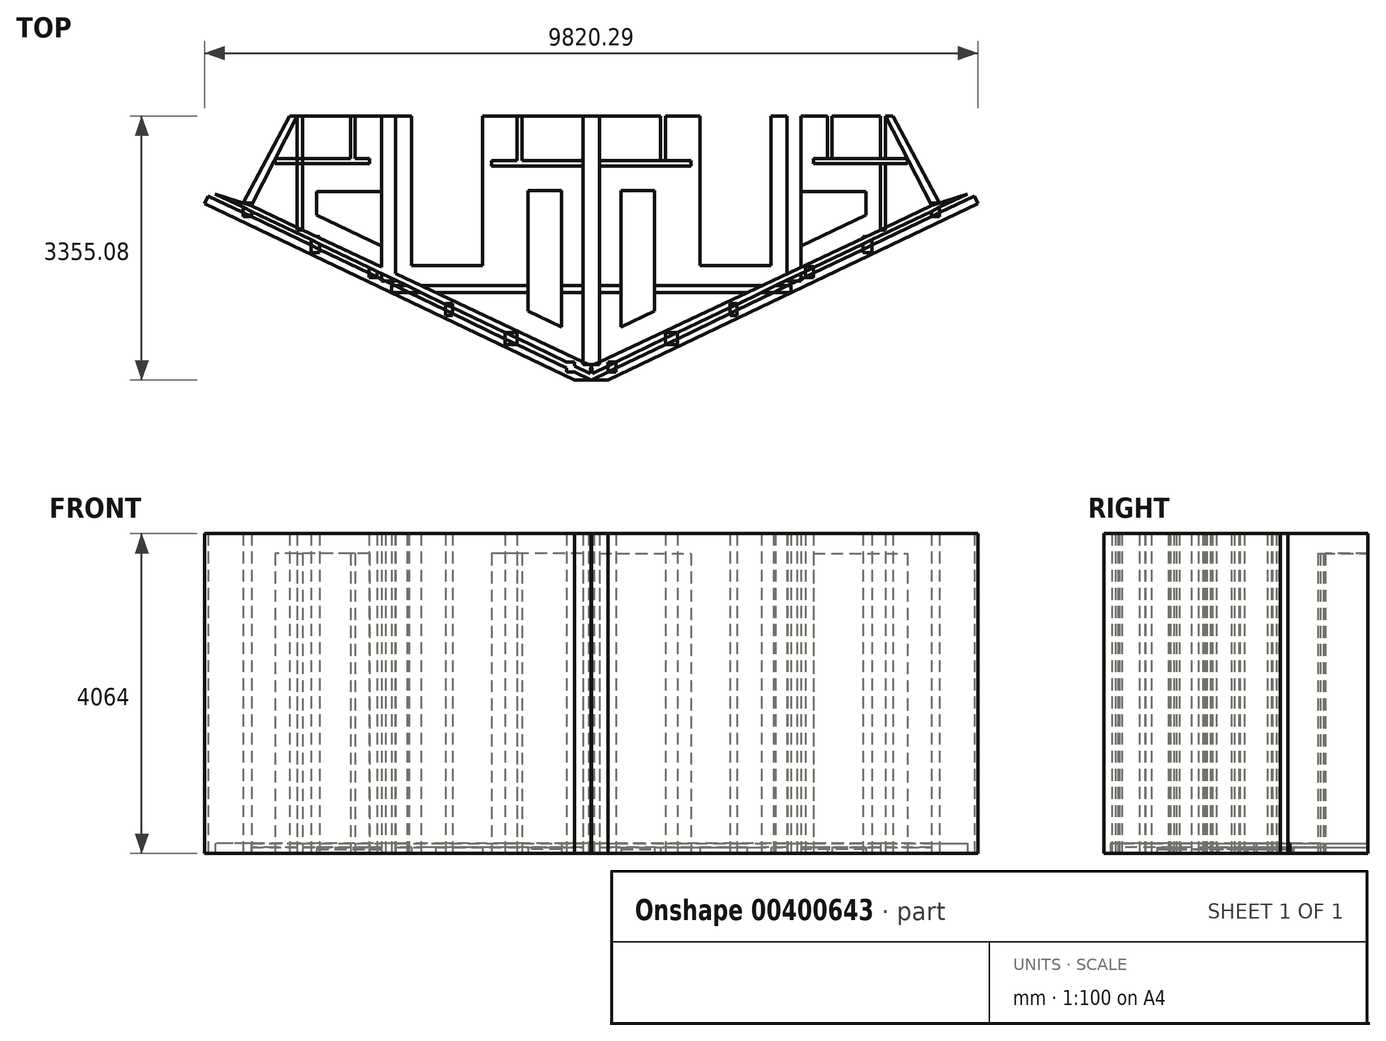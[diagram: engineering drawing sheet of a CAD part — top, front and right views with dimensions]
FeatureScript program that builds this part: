
annotation { "Feature Type Name" : "Feature", "Feature Type Description" : "" }
export const myFeature = defineFeature(function(context is Context, id is Id, definition is map)
    precondition{}
    {
        {
            var Q0;
            Q0=qCreatedBy(makeId("Top.planeOp"),FACE);
            var sketch = newSketch(context, id + "F0", { "sketchPlane" : qUnion([Q0])});
            skLineSegment(sketch, "E0", {"start": v(0, 0) * mm, "end": v(3734.31, 0) * mm});
            skLineSegment(sketch, "E1", {"start": v(3734.31, 0) * mm, "end": v(4319.25, -1139.54) * mm});
            skLineSegment(sketch, "E2", {"start": v(4319.25, -1139.54) * mm, "end": v(0, -3172.23) * mm});
            skLineSegment(sketch, "E3.bottom", {"start": v(1378.63, -1900) * mm, "end": v(2278.63, -1900) * mm});
            skLineSegment(sketch, "E3.top", {"start": v(1378.63, 0) * mm, "end": v(2278.63, 0) * mm});
            skLineSegment(sketch, "E3.left", {"start": v(1378.63, -1900) * mm, "end": v(1378.63, 0) * mm});
            skLineSegment(sketch, "E3.right", {"start": v(2278.63, -1900) * mm, "end": v(2278.63, 0) * mm});
            skLineSegment(sketch, "E4.bottom", {"start": v(3734.31, 0) * mm, "end": v(3668.02, 0) * mm});
            skLineSegment(sketch, "E4.top", {"start": v(3734.31, -1446.02) * mm, "end": v(3668.02, -1446.02) * mm});
            skLineSegment(sketch, "E4.left", {"start": v(3734.31, 0) * mm, "end": v(3734.31, -1446.02) * mm});
            skLineSegment(sketch, "E4.right", {"start": v(3668.02, 0) * mm, "end": v(3668.02, -1446.02) * mm});
            skLineSegment(sketch, "E5", {"start": v(12.4, -3268.41) * mm, "end": v(4773.75, -991.9) * mm});
            skLineSegment(sketch, "E6", {"start": v(4319.25, -1139.54) * mm, "end": v(4773.75, -991.9) * mm});
            skLineSegment(sketch, "E7", {"start": v(0, -3172.23) * mm, "end": v(12.4, -3268.41) * mm});
            skLineSegment(sketch, "E8.bottom", {"start": v(-2.48, -3156.82) * mm, "end": v(101.67, -3156.82) * mm});
            skLineSegment(sketch, "E8.top", {"start": v(-2.48, 0) * mm, "end": v(101.67, 0) * mm});
            skLineSegment(sketch, "E8.left", {"start": v(-2.48, -3156.82) * mm, "end": v(-2.48, 0) * mm});
            skLineSegment(sketch, "E8.right", {"start": v(101.67, -3156.82) * mm, "end": v(101.67, 0) * mm});
            skLineSegment(sketch, "E9.bottom", {"start": v(101.67, -567.84) * mm, "end": v(1262.25, -567.84) * mm});
            skLineSegment(sketch, "E9.top", {"start": v(101.67, -634.8) * mm, "end": v(1262.25, -634.8) * mm});
            skLineSegment(sketch, "E9.left", {"start": v(101.67, -567.84) * mm, "end": v(101.67, -634.8) * mm});
            skLineSegment(sketch, "E9.right", {"start": v(1262.25, -567.84) * mm, "end": v(1262.25, -634.8) * mm});
            skLineSegment(sketch, "E10.bottom", {"start": v(2817.13, -605.03) * mm, "end": v(4012.28, -605.03) * mm});
            skLineSegment(sketch, "E10.top", {"start": v(2817.13, -541.51) * mm, "end": v(4012.28, -541.51) * mm});
            skLineSegment(sketch, "E10.left", {"start": v(2817.13, -605.03) * mm, "end": v(2817.13, -541.51) * mm});
            skLineSegment(sketch, "E10.right", {"start": v(4012.28, -605.03) * mm, "end": v(4012.28, -541.51) * mm});
            skLineSegment(sketch, "E11.bottom", {"start": v(875.4, -567.84) * mm, "end": v(942.35, -567.84) * mm});
            skLineSegment(sketch, "E11.top", {"start": v(875.4, 0) * mm, "end": v(942.35, 0) * mm});
            skLineSegment(sketch, "E11.left", {"start": v(875.4, -567.84) * mm, "end": v(875.4, 0) * mm});
            skLineSegment(sketch, "E11.right", {"start": v(942.35, -567.84) * mm, "end": v(942.35, 0) * mm});
            skLineSegment(sketch, "E12.bottom", {"start": v(2995.68, -541.51) * mm, "end": v(3055.2, -541.51) * mm});
            skLineSegment(sketch, "E12.top", {"start": v(2995.68, 0) * mm, "end": v(3055.2, 0) * mm});
            skLineSegment(sketch, "E12.left", {"start": v(2995.68, -541.51) * mm, "end": v(2995.68, 0) * mm});
            skLineSegment(sketch, "E12.right", {"start": v(3055.2, -541.51) * mm, "end": v(3055.2, 0) * mm});
            skPoint(sketch, "E13.oppositeSnap0", {"position": v(2159.62, -2155.89) * mm});
            skLineSegment(sketch, "E13.bottom", {"start": v(101.67, -2241.75) * mm, "end": v(2534.42, -2241.75) * mm});
            skLineSegment(sketch, "E13.top", {"start": v(101.67, -2155.89) * mm, "end": v(2534.42, -2155.89) * mm});
            skLineSegment(sketch, "E13.left", {"start": v(101.67, -2241.75) * mm, "end": v(101.67, -2155.89) * mm});
            skLineSegment(sketch, "E13.right", {"start": v(2534.42, -2241.75) * mm, "end": v(2534.42, -2155.89) * mm});
            skLineSegment(sketch, "E14", {"start": v(4907.66, -1110.93) * mm, "end": v(4863.02, -1014.21) * mm});
            skLineSegment(sketch, "E15", {"start": v(4863.02, -1014.21) * mm, "end": v(0, -3355.08) * mm});
            skLineSegment(sketch, "E16", {"start": v(0, -3355.08) * mm, "end": v(210.83, -3355.08) * mm});
            skLineSegment(sketch, "E17", {"start": v(210.83, -3355.08) * mm, "end": v(4907.66, -1110.93) * mm});
            skLineSegment(sketch, "E18.bottom", {"start": v(210.83, -3253.6) * mm, "end": v(312.92, -3253.6) * mm});
            skLineSegment(sketch, "E18.top", {"start": v(210.83, -3124.73) * mm, "end": v(312.92, -3124.73) * mm});
            skLineSegment(sketch, "E18.left", {"start": v(210.83, -3253.6) * mm, "end": v(210.83, -3124.73) * mm});
            skLineSegment(sketch, "E18.right", {"start": v(312.92, -3253.6) * mm, "end": v(312.92, -3124.73) * mm});
            skLineSegment(sketch, "E19.bottom", {"start": v(942.92, -2901.2) * mm, "end": v(1090.07, -2901.2) * mm});
            skLineSegment(sketch, "E19.top", {"start": v(942.92, -2753.15) * mm, "end": v(1090.07, -2753.15) * mm});
            skLineSegment(sketch, "E19.left", {"start": v(942.92, -2901.2) * mm, "end": v(942.92, -2753.15) * mm});
            skLineSegment(sketch, "E19.right", {"start": v(1090.07, -2901.2) * mm, "end": v(1090.07, -2753.15) * mm});
            skLineSegment(sketch, "E20.bottom", {"start": v(1758.25, -2534.14) * mm, "end": v(1845.43, -2534.14) * mm});
            skLineSegment(sketch, "E20.top", {"start": v(1758.25, -2381.58) * mm, "end": v(1845.43, -2381.58) * mm});
            skLineSegment(sketch, "E20.left", {"start": v(1758.25, -2534.14) * mm, "end": v(1758.25, -2381.58) * mm});
            skLineSegment(sketch, "E20.right", {"start": v(1845.43, -2534.14) * mm, "end": v(1845.43, -2381.58) * mm});
            skLineSegment(sketch, "E21.bottom", {"start": v(2717.22, -2054.65) * mm, "end": v(2818.93, -2054.65) * mm});
            skLineSegment(sketch, "E21.top", {"start": v(2717.22, -1909.36) * mm, "end": v(2818.93, -1909.36) * mm});
            skLineSegment(sketch, "E21.left", {"start": v(2717.22, -2054.65) * mm, "end": v(2717.22, -1909.36) * mm});
            skLineSegment(sketch, "E21.right", {"start": v(2818.93, -2054.65) * mm, "end": v(2818.93, -1909.36) * mm});
            skLineSegment(sketch, "E22.bottom", {"start": v(3450.98, -1735) * mm, "end": v(3559.95, -1735) * mm});
            skLineSegment(sketch, "E22.top", {"start": v(3450.98, -1531.58) * mm, "end": v(3559.95, -1531.58) * mm});
            skLineSegment(sketch, "E22.left", {"start": v(3450.98, -1735) * mm, "end": v(3450.98, -1531.58) * mm});
            skLineSegment(sketch, "E22.right", {"start": v(3559.95, -1735) * mm, "end": v(3559.95, -1531.58) * mm});
            skLineSegment(sketch, "E23.bottom", {"start": v(2484.75, -2098.24) * mm, "end": v(2659.1, -2098.24) * mm});
            skLineSegment(sketch, "E23.top", {"start": v(2484.75, 0) * mm, "end": v(2659.1, 0) * mm});
            skLineSegment(sketch, "E23.left", {"start": v(2484.75, -2098.24) * mm, "end": v(2484.75, 0) * mm});
            skLineSegment(sketch, "E23.right", {"start": v(2659.1, -2098.24) * mm, "end": v(2659.1, 0) * mm});
            skLineSegment(sketch, "E24", {"start": v(4422.89, -1105.87) * mm, "end": v(3828.76, 0) * mm});
            skLineSegment(sketch, "E25", {"start": v(3734.31, 0) * mm, "end": v(3828.76, 0) * mm});
            skLineSegment(sketch, "E26.bottom", {"start": v(4315.69, -1277.68) * mm, "end": v(4422.89, -1277.68) * mm});
            skLineSegment(sketch, "E26.top", {"start": v(4315.69, -1105.87) * mm, "end": v(4422.89, -1105.87) * mm});
            skLineSegment(sketch, "E26.left", {"start": v(4315.69, -1277.68) * mm, "end": v(4315.69, -1105.87) * mm});
            skLineSegment(sketch, "E26.right", {"start": v(4422.89, -1277.68) * mm, "end": v(4422.89, -1105.87) * mm});
            skLineSegment(sketch, "E27.MirrorCS", {"start": v(-3739.28, 0) * mm, "end": v(-3672.98, 0) * mm});
            skLineSegment(sketch, "E28.MirrorCS", {"start": v(-4320.65, -1105.87) * mm, "end": v(-4427.85, -1105.87) * mm});
            skLineSegment(sketch, "E29.MirrorCS", {"start": v(-1763.22, -2534.14) * mm, "end": v(-1850.4, -2534.14) * mm});
            skLineSegment(sketch, "E30.MirrorCS", {"start": v(-4017.24, -605.03) * mm, "end": v(-4017.24, -541.51) * mm});
            skLineSegment(sketch, "E31.MirrorCS", {"start": v(-1095.04, -2901.2) * mm, "end": v(-1095.04, -2753.15) * mm});
            skLineSegment(sketch, "E32.MirrorCS", {"start": v(-2823.9, -2054.65) * mm, "end": v(-2823.9, -1909.36) * mm});
            skLineSegment(sketch, "E33.MirrorCS", {"start": v(-3455.95, -1735) * mm, "end": v(-3564.92, -1735) * mm});
            skLineSegment(sketch, "E34.MirrorCS", {"start": v(-215.8, -3253.6) * mm, "end": v(-317.88, -3253.6) * mm});
            skLineSegment(sketch, "E35.MirrorCS", {"start": v(-880.36, -567.84) * mm, "end": v(-947.31, -567.84) * mm});
            skLineSegment(sketch, "E36.MirrorCS", {"start": v(-3739.28, 0) * mm, "end": v(-3833.72, 0) * mm});
            skLineSegment(sketch, "E37.MirrorCS", {"start": v(-1763.22, -2381.58) * mm, "end": v(-1850.4, -2381.58) * mm});
            skLineSegment(sketch, "E38.MirrorCS", {"start": v(-2822.1, -605.03) * mm, "end": v(-2822.1, -541.51) * mm});
            skLineSegment(sketch, "E39.MirrorCS", {"start": v(-2722.2, -2054.65) * mm, "end": v(-2722.2, -1909.36) * mm});
            skLineSegment(sketch, "E40.MirrorCS", {"start": v(-947.89, -2901.2) * mm, "end": v(-947.89, -2753.15) * mm});
            skLineSegment(sketch, "E41.MirrorCS", {"start": v(-2489.71, 0) * mm, "end": v(-2664.07, 0) * mm});
            skLineSegment(sketch, "E42.MirrorCS", {"start": v(-947.89, -2753.15) * mm, "end": v(-1095.04, -2753.15) * mm});
            skLineSegment(sketch, "E43.MirrorCS", {"start": v(-4320.65, -1277.68) * mm, "end": v(-4320.65, -1105.87) * mm});
            skLineSegment(sketch, "E44.MirrorCS", {"start": v(-3000.65, 0) * mm, "end": v(-3060.16, 0) * mm});
            skLineSegment(sketch, "E45.MirrorCS", {"start": v(-4912.63, -1110.93) * mm, "end": v(-4867.99, -1014.21) * mm});
            skLineSegment(sketch, "E46.MirrorCS", {"start": v(-215.8, -3124.73) * mm, "end": v(-317.88, -3124.73) * mm});
            skLineSegment(sketch, "E47.MirrorCS", {"start": v(-4.97, -3172.23) * mm, "end": v(-17.36, -3268.41) * mm});
            skLineSegment(sketch, "E48.MirrorCS", {"start": v(-2722.2, -2054.65) * mm, "end": v(-2823.9, -2054.65) * mm});
            skLineSegment(sketch, "E49.MirrorCS", {"start": v(-106.64, -567.84) * mm, "end": v(-106.64, -634.8) * mm});
            skLineSegment(sketch, "E50.MirrorCS", {"start": v(-2.48, 0) * mm, "end": v(-106.64, 0) * mm});
            skLineSegment(sketch, "E51.MirrorCS", {"start": v(-2.48, -3156.82) * mm, "end": v(-106.64, -3156.82) * mm});
            skLineSegment(sketch, "E52.MirrorCS", {"start": v(-317.88, -3253.6) * mm, "end": v(-317.88, -3124.73) * mm});
            skLineSegment(sketch, "E53.MirrorCS", {"start": v(-880.36, 0) * mm, "end": v(-947.31, 0) * mm});
            skLineSegment(sketch, "E54.MirrorCS", {"start": v(-4427.85, -1277.68) * mm, "end": v(-4427.85, -1105.87) * mm});
            skLineSegment(sketch, "E55.MirrorCS", {"start": v(-2722.2, -1909.36) * mm, "end": v(-2823.9, -1909.36) * mm});
            skLineSegment(sketch, "E56.MirrorCS", {"start": v(-4320.65, -1277.68) * mm, "end": v(-4427.85, -1277.68) * mm});
            skLineSegment(sketch, "E57.MirrorCS", {"start": v(-1763.22, -2534.14) * mm, "end": v(-1763.22, -2381.58) * mm});
            skLineSegment(sketch, "E58.MirrorCS", {"start": v(-106.64, -2241.75) * mm, "end": v(-106.64, -2155.89) * mm});
            skLineSegment(sketch, "E59.MirrorCS", {"start": v(-3739.28, -1446.02) * mm, "end": v(-3672.98, -1446.02) * mm});
            skLineSegment(sketch, "E60.MirrorCS", {"start": v(-3455.95, -1531.58) * mm, "end": v(-3564.92, -1531.58) * mm});
            skLineSegment(sketch, "E61.MirrorCS", {"start": v(-3000.65, -541.51) * mm, "end": v(-3060.16, -541.51) * mm});
            skLineSegment(sketch, "E62.MirrorCS", {"start": v(-215.8, -3253.6) * mm, "end": v(-215.8, -3124.73) * mm});
            skLineSegment(sketch, "E63.MirrorCS", {"start": v(-1267.22, -567.84) * mm, "end": v(-1267.22, -634.8) * mm});
            skLineSegment(sketch, "E64.MirrorCS", {"start": v(-1850.4, -2534.14) * mm, "end": v(-1850.4, -2381.58) * mm});
            skLineSegment(sketch, "E65.MirrorCS", {"start": v(-2489.71, -2098.24) * mm, "end": v(-2664.07, -2098.24) * mm});
            skLineSegment(sketch, "E66.MirrorCS", {"start": v(-947.89, -2901.2) * mm, "end": v(-1095.04, -2901.2) * mm});
            skLineSegment(sketch, "E67.MirrorCS", {"start": v(-2539.4, -2241.75) * mm, "end": v(-2539.4, -2155.89) * mm});
            skLineSegment(sketch, "E68.MirrorCS", {"start": v(-3564.92, -1735) * mm, "end": v(-3564.92, -1531.58) * mm});
            skLineSegment(sketch, "E69.MirrorCS", {"start": v(-3455.95, -1735) * mm, "end": v(-3455.95, -1531.58) * mm});
            skLineSegment(sketch, "E70.MirrorCS", {"start": v(-106.64, -2241.75) * mm, "end": v(-2539.4, -2241.75) * mm});
            skLineSegment(sketch, "E71.MirrorCS", {"start": v(-4427.85, -1105.87) * mm, "end": v(-3833.72, 0) * mm});
            skLineSegment(sketch, "E72.MirrorCS", {"start": v(-106.64, -567.84) * mm, "end": v(-1267.22, -567.84) * mm});
            skLineSegment(sketch, "E73.MirrorCS", {"start": v(-3060.16, -541.51) * mm, "end": v(-3060.16, 0) * mm});
            skLineSegment(sketch, "E74.MirrorCS", {"start": v(-2664.07, -2098.24) * mm, "end": v(-2664.07, 0) * mm});
            skLineSegment(sketch, "E75.MirrorCS", {"start": v(-106.64, -634.8) * mm, "end": v(-1267.22, -634.8) * mm});
            skLineSegment(sketch, "E76.MirrorCS", {"start": v(-106.64, -3156.82) * mm, "end": v(-106.64, 0) * mm});
            skLineSegment(sketch, "E77.MirrorCS", {"start": v(-4.97, -3355.08) * mm, "end": v(-215.8, -3355.08) * mm});
            skLineSegment(sketch, "E78.MirrorCS", {"start": v(-106.64, -2155.89) * mm, "end": v(-2539.4, -2155.89) * mm});
            skLineSegment(sketch, "E79.MirrorCS", {"start": v(-215.8, -3355.08) * mm, "end": v(-4912.63, -1110.93) * mm});
            skLineSegment(sketch, "E80.MirrorCS", {"start": v(-3000.65, -541.51) * mm, "end": v(-3000.65, 0) * mm});
            skLineSegment(sketch, "E81.MirrorCS", {"start": v(-2489.71, -2098.24) * mm, "end": v(-2489.71, 0) * mm});
            skPoint(sketch, "E82.MirrorP", {"position": v(-2164.6, -2155.89) * mm});
            skLineSegment(sketch, "E83.MirrorCS", {"start": v(-2822.1, -605.03) * mm, "end": v(-4017.24, -605.03) * mm});
            skLineSegment(sketch, "E84.MirrorCS", {"start": v(-4.97, 0) * mm, "end": v(-3739.28, 0) * mm});
            skLineSegment(sketch, "E85.MirrorCS", {"start": v(-3739.28, 0) * mm, "end": v(-4324.22, -1139.54) * mm});
            skLineSegment(sketch, "E86.MirrorCS", {"start": v(-4324.22, -1139.54) * mm, "end": v(-4.97, -3172.23) * mm});
            skLineSegment(sketch, "E87.MirrorCS", {"start": v(-4867.99, -1014.21) * mm, "end": v(-4.97, -3355.08) * mm});
            skLineSegment(sketch, "E88.MirrorCS", {"start": v(-2822.1, -541.51) * mm, "end": v(-4017.24, -541.51) * mm});
            skLineSegment(sketch, "E89.MirrorCS", {"start": v(-1383.6, -1900) * mm, "end": v(-2283.6, -1900) * mm});
            skLineSegment(sketch, "E90.MirrorCS", {"start": v(-947.31, -567.84) * mm, "end": v(-947.31, 0) * mm});
            skLineSegment(sketch, "E91.MirrorCS", {"start": v(-1383.6, 0) * mm, "end": v(-2283.6, 0) * mm});
            skLineSegment(sketch, "E92.MirrorCS", {"start": v(-4324.22, -1139.54) * mm, "end": v(-4778.71, -991.9) * mm});
            skLineSegment(sketch, "E93.MirrorCS", {"start": v(-17.36, -3268.41) * mm, "end": v(-4778.71, -991.9) * mm});
            skLineSegment(sketch, "E94.MirrorCS", {"start": v(-3739.28, 0) * mm, "end": v(-3739.28, -1446.02) * mm});
            skLineSegment(sketch, "E95.MirrorCS", {"start": v(-2283.6, -1900) * mm, "end": v(-2283.6, 0) * mm});
            skLineSegment(sketch, "E96.MirrorCS", {"start": v(-1383.6, -1900) * mm, "end": v(-1383.6, 0) * mm});
            skLineSegment(sketch, "E97.MirrorCS", {"start": v(-3672.98, 0) * mm, "end": v(-3672.98, -1446.02) * mm});
            skLineSegment(sketch, "E98.MirrorCS", {"start": v(-880.36, -567.84) * mm, "end": v(-880.36, 0) * mm});
            skLineSegment(sketch, "E99", {"start": v(-383, -2677.78) * mm, "end": v(-383, -949.63) * mm});
            skLineSegment(sketch, "E100", {"start": v(-383, -949.63) * mm, "end": v(-804.7, -949.63) * mm});
            skLineSegment(sketch, "E101", {"start": v(-804.7, -949.63) * mm, "end": v(-804.7, -2476.29) * mm});
            skLineSegment(sketch, "E102", {"start": v(-804.7, -2476.29) * mm, "end": v(-383, -2677.78) * mm});
            skPoint(sketch, "E103.endSnap0", {"position": v(-3419.67, -605.03) * mm});
            skLineSegment(sketch, "E104", {"start": v(-3492.38, -1256.21) * mm, "end": v(-2664.07, -1654.93) * mm});
            skLineSegment(sketch, "E105", {"start": v(-3492.38, -1256.21) * mm, "end": v(-3492.38, -959.85) * mm});
            skLineSegment(sketch, "E106", {"start": v(-3492.38, -959.85) * mm, "end": v(-2664.07, -959.85) * mm});
            skLineSegment(sketch, "E107.MirrorCS", {"start": v(799.73, -949.63) * mm, "end": v(799.73, -2476.29) * mm});
            skLineSegment(sketch, "E108.MirrorCS", {"start": v(378.03, -2677.78) * mm, "end": v(378.03, -949.63) * mm});
            skLineSegment(sketch, "E109.MirrorCS", {"start": v(378.03, -949.63) * mm, "end": v(799.73, -949.63) * mm});
            skLineSegment(sketch, "E110.MirrorCS", {"start": v(799.73, -2476.29) * mm, "end": v(378.03, -2677.78) * mm});
            skLineSegment(sketch, "E111.MirrorCS", {"start": v(3487.42, -1256.21) * mm, "end": v(2659.1, -1654.93) * mm});
            skLineSegment(sketch, "E112.MirrorCS", {"start": v(3487.42, -1256.21) * mm, "end": v(3487.42, -959.85) * mm});
            skLineSegment(sketch, "E113.MirrorCS", {"start": v(3487.42, -959.85) * mm, "end": v(2659.1, -959.85) * mm});
            skSolve(sketch);
        }
        {
            var Q0;
            {var subQ1=sQuery(id+"F0.wireOp",EDGE,"E28.MirrorCS");Q0=makeQuery(id+"F0.imprint","IMPRINT",FACE,{"disambiguationData":[TD([[makeQuery(id+"F0.imprint","IMPRINT",EDGE,{"derivedFrom":subQ1}),-1.0]])]});}
            var Q1;
            {var subQ5=sQuery(id+"F0.wireOp",EDGE,"E29.MirrorCS");Q1=makeQuery(id+"F0.imprint","IMPRINT",FACE,{"disambiguationData":[TD([[makeQuery(id+"F0.imprint","IMPRINT",EDGE,{"derivedFrom":subQ5}),1.0]])]});}
            var Q2;
            {var subQ20=sQuery(id+"F0.wireOp",EDGE,"E13.right");Q2=makeQuery(id+"F0.imprint","IMPRINT",FACE,{"disambiguationData":[TD([[makeQuery(id+"F0.imprint","IMPRINT",EDGE,{"derivedFrom":subQ20}),-1.0]])]});}
            var Q3;
            Q3=makeQuery(id+"F0.imprint","IMPRINT",FACE,{"disambiguationData":[TD([[makeQuery(id+"F0.imprint","IMPRINT",EDGE,{"derivedFrom":sQuery(id+"F0.wireOp",EDGE,"E24")}),1.0]])]});
            var Q4;
            {var subQ5=sQuery(id+"F0.wireOp",EDGE,"E8.left");Q4=makeQuery(id+"F0.imprint","IMPRINT",FACE,{"disambiguationData":[TD([[makeQuery(id+"F0.imprint","IMPRINT",EDGE,{"derivedFrom":subQ5}),1.0]])]});}
            var Q5;
            {var subQ3=sQuery(id+"F0.wireOp",EDGE,"E8.left");Q5=makeQuery(id+"F0.imprint","IMPRINT",FACE,{"disambiguationData":[TD([[makeQuery(id+"F0.imprint","IMPRINT",EDGE,{"derivedFrom":subQ3}),-1.0]])]});}
            extrude(context, id + "F1", {"entities" : qUnion([Q0, Q1, Q2, Q3, Q4, Q5]), "depth" : 4064 * mm, "offsetDistance" : 25.4 * mm});
        }
        {
            var Q0;
            {var subQ1=sQuery(id+"F0.wireOp",EDGE,"E5");var subQ3=sQuery(id+"F0.wireOp",EDGE,"E18.left");var subQ4=makeQuery(id+"F0.imprint","INTERSECT",VERTEX,{"derivedFrom":[subQ1,subQ3]});Q0=makeQuery(id+"F0.imprint","IMPRINT",FACE,{"disambiguationData":[TD([[makeQuery(id+"F0.imprint","IMPRINT",EDGE,{"disambiguationData":[TD([[subQ4,-1.0]])],"derivedFrom":subQ1}),-1.0]])]});}
            var Q1;
            {var subQ1=sQuery(id+"F0.wireOp",EDGE,"E5");var subQ3=sQuery(id+"F0.wireOp",EDGE,"E19.left");var subQ4=makeQuery(id+"F0.imprint","INTERSECT",VERTEX,{"derivedFrom":[subQ1,subQ3]});Q1=makeQuery(id+"F0.imprint","IMPRINT",FACE,{"disambiguationData":[TD([[makeQuery(id+"F0.imprint","IMPRINT",EDGE,{"disambiguationData":[TD([[subQ4,-1.0]])],"derivedFrom":subQ1}),-1.0]])]});}
            var Q2;
            {var subQ0=sQuery(id+"F0.wireOp",EDGE,"E20.left");var subQ1=sQuery(id+"F0.wireOp",EDGE,"E5");var subQ2=makeQuery(id+"F0.imprint","INTERSECT",VERTEX,{"derivedFrom":[subQ1,subQ0]});Q2=makeQuery(id+"F0.imprint","IMPRINT",FACE,{"disambiguationData":[TD([[makeQuery(id+"F0.imprint","IMPRINT",EDGE,{"disambiguationData":[TD([[subQ2,-1.0]])],"derivedFrom":subQ1}),-1.0]])]});}
            var Q3;
            {var subQ0=sQuery(id+"F0.wireOp",EDGE,"E13.bottom");var subQ1=sQuery(id+"F0.wireOp",EDGE,"E5");var subQ2=makeQuery(id+"F0.imprint","INTERSECT",VERTEX,{"derivedFrom":[subQ1,subQ0]});Q3=makeQuery(id+"F0.imprint","IMPRINT",FACE,{"disambiguationData":[TD([[makeQuery(id+"F0.imprint","IMPRINT",EDGE,{"disambiguationData":[TD([[subQ2,-1.0]])],"derivedFrom":subQ1}),-1.0]])]});}
            var Q4;
            {var subQ0=sQuery(id+"F0.wireOp",EDGE,"E21.left");var subQ1=sQuery(id+"F0.wireOp",EDGE,"E5");var subQ2=makeQuery(id+"F0.imprint","INTERSECT",VERTEX,{"derivedFrom":[subQ1,subQ0]});Q4=makeQuery(id+"F0.imprint","IMPRINT",FACE,{"disambiguationData":[TD([[makeQuery(id+"F0.imprint","IMPRINT",EDGE,{"disambiguationData":[TD([[subQ2,-1.0]])],"derivedFrom":subQ1}),-1.0]])]});}
            var Q5;
            {var subQ0=sQuery(id+"F0.wireOp",EDGE,"E22.left");var subQ1=sQuery(id+"F0.wireOp",EDGE,"E5");var subQ2=makeQuery(id+"F0.imprint","INTERSECT",VERTEX,{"derivedFrom":[subQ1,subQ0]});Q5=makeQuery(id+"F0.imprint","IMPRINT",FACE,{"disambiguationData":[TD([[makeQuery(id+"F0.imprint","IMPRINT",EDGE,{"disambiguationData":[TD([[subQ2,-1.0]])],"derivedFrom":subQ1}),-1.0]])]});}
            var Q6;
            {var subQ0=sQuery(id+"F0.wireOp",EDGE,"E26.right");var subQ1=sQuery(id+"F0.wireOp",EDGE,"E5");var subQ2=makeQuery(id+"F0.imprint","INTERSECT",VERTEX,{"derivedFrom":[subQ1,subQ0]});Q6=makeQuery(id+"F0.imprint","IMPRINT",FACE,{"disambiguationData":[TD([[makeQuery(id+"F0.imprint","IMPRINT",EDGE,{"disambiguationData":[TD([[subQ2,1.0]])],"derivedFrom":subQ1}),-1.0]])]});}
            var Q7;
            {var subQ1=sQuery(id+"F0.wireOp",EDGE,"E31.MirrorCS");var subQ3=sQuery(id+"F0.wireOp",EDGE,"E87.MirrorCS");var subQ4=makeQuery(id+"F0.imprint","INTERSECT",VERTEX,{"derivedFrom":[subQ1,subQ3]});Q7=makeQuery(id+"F0.imprint","IMPRINT",FACE,{"disambiguationData":[TD([[makeQuery(id+"F0.imprint","IMPRINT",EDGE,{"disambiguationData":[TD([[subQ4,-1.0]])],"derivedFrom":subQ1}),-1.0]])]});}
            var Q8;
            {var subQ0=sQuery(id+"F0.wireOp",EDGE,"E87.MirrorCS");var subQ1=sQuery(id+"F0.wireOp",EDGE,"E57.MirrorCS");var subQ2=makeQuery(id+"F0.imprint","INTERSECT",VERTEX,{"derivedFrom":[subQ1,subQ0]});Q8=makeQuery(id+"F0.imprint","IMPRINT",FACE,{"disambiguationData":[TD([[makeQuery(id+"F0.imprint","IMPRINT",EDGE,{"disambiguationData":[TD([[subQ2,-1.0]])],"derivedFrom":subQ1}),1.0]])]});}
            var Q9;
            {var subQ0=sQuery(id+"F0.wireOp",EDGE,"E93.MirrorCS");var subQ1=sQuery(id+"F0.wireOp",EDGE,"E70.MirrorCS");var subQ2=makeQuery(id+"F0.imprint","INTERSECT",VERTEX,{"derivedFrom":[subQ1,subQ0]});Q9=makeQuery(id+"F0.imprint","IMPRINT",FACE,{"disambiguationData":[TD([[makeQuery(id+"F0.imprint","IMPRINT",EDGE,{"disambiguationData":[TD([[subQ2,-1.0]])],"derivedFrom":subQ1}),-1.0]])]});}
            var Q10;
            {var subQ0=sQuery(id+"F0.wireOp",EDGE,"E87.MirrorCS");var subQ1=sQuery(id+"F0.wireOp",EDGE,"E32.MirrorCS");var subQ2=makeQuery(id+"F0.imprint","INTERSECT",VERTEX,{"derivedFrom":[subQ1,subQ0]});Q10=makeQuery(id+"F0.imprint","IMPRINT",FACE,{"disambiguationData":[TD([[makeQuery(id+"F0.imprint","IMPRINT",EDGE,{"disambiguationData":[TD([[subQ2,-1.0]])],"derivedFrom":subQ1}),-1.0]])]});}
            var Q11;
            {var subQ1=sQuery(id+"F0.wireOp",EDGE,"E65.MirrorCS");var subQ5=sQuery(id+"F0.wireOp",EDGE,"E81.MirrorCS");var subQ6=makeQuery(id+"F0.imprint","INTERSECT",VERTEX,{"derivedFrom":[subQ1,subQ5]});Q11=makeQuery(id+"F0.imprint","IMPRINT",FACE,{"disambiguationData":[TD([[makeQuery(id+"F0.imprint","IMPRINT",EDGE,{"disambiguationData":[TD([[subQ6,-1.0]])],"derivedFrom":subQ1}),-1.0]])]});}
            var Q12;
            {var subQ0=sQuery(id+"F0.wireOp",EDGE,"E23.left");var subQ3=sQuery(id+"F0.wireOp",EDGE,"E5");var subQ4=makeQuery(id+"F0.imprint","INTERSECT",VERTEX,{"derivedFrom":[subQ3,subQ0]});Q12=makeQuery(id+"F0.imprint","IMPRINT",FACE,{"disambiguationData":[TD([[makeQuery(id+"F0.imprint","IMPRINT",EDGE,{"disambiguationData":[TD([[subQ4,-1.0]])],"derivedFrom":subQ3}),-1.0]])]});}
            var Q13;
            {var subQ0=sQuery(id+"F0.wireOp",EDGE,"E87.MirrorCS");var subQ1=sQuery(id+"F0.wireOp",EDGE,"E68.MirrorCS");var subQ2=makeQuery(id+"F0.imprint","INTERSECT",VERTEX,{"derivedFrom":[subQ1,subQ0]});Q13=makeQuery(id+"F0.imprint","IMPRINT",FACE,{"disambiguationData":[TD([[makeQuery(id+"F0.imprint","IMPRINT",EDGE,{"disambiguationData":[TD([[subQ2,-1.0]])],"derivedFrom":subQ1}),-1.0]])]});}
            var Q14;
            {var subQ0=sQuery(id+"F0.wireOp",EDGE,"E87.MirrorCS");var subQ5=sQuery(id+"F0.wireOp",EDGE,"E54.MirrorCS");var subQ6=makeQuery(id+"F0.imprint","INTERSECT",VERTEX,{"derivedFrom":[subQ5,subQ0]});Q14=makeQuery(id+"F0.imprint","IMPRINT",FACE,{"disambiguationData":[TD([[makeQuery(id+"F0.imprint","IMPRINT",EDGE,{"disambiguationData":[TD([[subQ6,-1.0]])],"derivedFrom":subQ5}),-1.0]])]});}
            extrude(context, id + "F2", {"entities" : qUnion([Q0, Q1, Q2, Q3, Q4, Q5, Q6, Q7, Q8, Q9, Q10, Q11, Q12, Q13, Q14]), "depth" : 4064 * mm, "offsetDistance" : 25.4 * mm});
        }
        {
            var Q0;
            {var subQ4=sQuery(id+"F0.wireOp",EDGE,"E38.MirrorCS");Q0=makeQuery(id+"F0.imprint","IMPRINT",FACE,{"disambiguationData":[TD([[makeQuery(id+"F0.imprint","IMPRINT",EDGE,{"derivedFrom":subQ4}),1.0]])]});}
            var Q1;
            {var subQ0=sQuery(id+"F0.wireOp",EDGE,"E30.MirrorCS");Q1=makeQuery(id+"F0.imprint","IMPRINT",FACE,{"disambiguationData":[TD([[makeQuery(id+"F0.imprint","IMPRINT",EDGE,{"derivedFrom":subQ0}),-1.0]])]});}
            var Q2;
            {var subQ0=sQuery(id+"F0.wireOp",EDGE,"E73.MirrorCS");Q2=makeQuery(id+"F0.imprint","IMPRINT",FACE,{"disambiguationData":[TD([[makeQuery(id+"F0.imprint","IMPRINT",EDGE,{"derivedFrom":subQ0}),-1.0]])]});}
            var Q3;
            {var subQ3=sQuery(id+"F0.wireOp",EDGE,"E97.MirrorCS");var subQ5=sQuery(id+"F0.wireOp",EDGE,"E88.MirrorCS");var subQ6=makeQuery(id+"F0.imprint","INTERSECT",VERTEX,{"derivedFrom":[subQ5,subQ3]});Q3=makeQuery(id+"F0.imprint","IMPRINT",FACE,{"disambiguationData":[TD([[makeQuery(id+"F0.imprint","IMPRINT",EDGE,{"disambiguationData":[TD([[subQ6,-1.0]])],"derivedFrom":subQ5}),-1.0]])]});}
            var Q4;
            {var subQ1=sQuery(id+"F0.wireOp",EDGE,"E63.MirrorCS");Q4=makeQuery(id+"F0.imprint","IMPRINT",FACE,{"disambiguationData":[TD([[makeQuery(id+"F0.imprint","IMPRINT",EDGE,{"derivedFrom":subQ1}),1.0]])]});}
            var Q5;
            Q5=makeQuery(id+"F0.imprint","IMPRINT",FACE,{"disambiguationData":[TD([[makeQuery(id+"F0.imprint","IMPRINT",EDGE,{"derivedFrom":sQuery(id+"F0.wireOp",EDGE,"E9.top")}),1.0]])]});
            var Q6;
            Q6=makeQuery(id+"F0.imprint","IMPRINT",FACE,{"disambiguationData":[TD([[makeQuery(id+"F0.imprint","IMPRINT",EDGE,{"derivedFrom":sQuery(id+"F0.wireOp",EDGE,"E11.bottom")}),1.0]])]});
            var Q7;
            Q7=makeQuery(id+"F0.imprint","IMPRINT",FACE,{"disambiguationData":[TD([[makeQuery(id+"F0.imprint","IMPRINT",EDGE,{"derivedFrom":sQuery(id+"F0.wireOp",EDGE,"E12.bottom")}),1.0]])]});
            var Q8;
            {var subQ4=sQuery(id+"F0.wireOp",EDGE,"E10.left");Q8=makeQuery(id+"F0.imprint","IMPRINT",FACE,{"disambiguationData":[TD([[makeQuery(id+"F0.imprint","IMPRINT",EDGE,{"derivedFrom":subQ4}),-1.0]])]});}
            var Q9;
            {var subQ5=sQuery(id+"F0.wireOp",EDGE,"E10.right");Q9=makeQuery(id+"F0.imprint","IMPRINT",FACE,{"disambiguationData":[TD([[makeQuery(id+"F0.imprint","IMPRINT",EDGE,{"derivedFrom":subQ5}),1.0]])]});}
            var Q10;
            {var subQ0=sQuery(id+"F0.wireOp",EDGE,"E10.top");var subQ1=sQuery(id+"F0.wireOp",EDGE,"E4.left");var subQ2=makeQuery(id+"F0.imprint","INTERSECT",VERTEX,{"derivedFrom":[subQ1,subQ0]});Q10=makeQuery(id+"F0.imprint","IMPRINT",FACE,{"disambiguationData":[TD([[makeQuery(id+"F0.imprint","IMPRINT",EDGE,{"disambiguationData":[TD([[subQ2,-1.0]])],"derivedFrom":subQ1}),-1.0]])]});}
            var Q11;
            {var subQ0=sQuery(id+"F0.wireOp",EDGE,"E4.bottom");Q11=makeQuery(id+"F0.imprint","IMPRINT",FACE,{"disambiguationData":[TD([[makeQuery(id+"F0.imprint","IMPRINT",EDGE,{"derivedFrom":subQ0}),1.0]])]});}
            var Q12;
            {var subQ0=sQuery(id+"F0.wireOp",EDGE,"E90.MirrorCS");Q12=makeQuery(id+"F0.imprint","IMPRINT",FACE,{"disambiguationData":[TD([[makeQuery(id+"F0.imprint","IMPRINT",EDGE,{"derivedFrom":subQ0}),-1.0]])]});}
            extrude(context, id + "F3", {"entities" : qUnion([Q0, Q1, Q2, Q3, Q4, Q5, Q6, Q7, Q8, Q9, Q10, Q11, Q12]), "operationType" : NewBodyOperationType.ADD, "depth" : 3810 * mm, "offsetDistance" : 25.4 * mm});
        }
        {
            var Q0;
            {var subQ5=sQuery(id+"F0.wireOp",EDGE,"E23.top");Q0=makeQuery(id+"F0.imprint","IMPRINT",FACE,{"disambiguationData":[TD([[makeQuery(id+"F0.imprint","IMPRINT",EDGE,{"derivedFrom":subQ5}),-1.0]])]});}
            var Q1;
            {var subQ1=sQuery(id+"F0.wireOp",EDGE,"E3.top");Q1=makeQuery(id+"F0.imprint","IMPRINT",FACE,{"disambiguationData":[TD([[makeQuery(id+"F0.imprint","IMPRINT",EDGE,{"derivedFrom":subQ1}),-1.0]])]});}
            var Q2;
            {var subQ5=sQuery(id+"F0.wireOp",EDGE,"E13.left");Q2=makeQuery(id+"F0.imprint","IMPRINT",FACE,{"disambiguationData":[TD([[makeQuery(id+"F0.imprint","IMPRINT",EDGE,{"derivedFrom":subQ5}),-1.0]])]});}
            var Q3;
            {var subQ10=sQuery(id+"F0.wireOp",EDGE,"E7");Q3=makeQuery(id+"F0.imprint","IMPRINT",FACE,{"disambiguationData":[TD([[makeQuery(id+"F0.imprint","IMPRINT",EDGE,{"derivedFrom":subQ10}),1.0]])]});}
            var Q4;
            {var subQ3=sQuery(id+"F0.wireOp",EDGE,"E2");var subQ5=sQuery(id+"F0.wireOp",EDGE,"E23.left");var subQ6=makeQuery(id+"F0.imprint","INTERSECT",VERTEX,{"derivedFrom":[subQ3,subQ5]});Q4=makeQuery(id+"F0.imprint","IMPRINT",FACE,{"disambiguationData":[TD([[makeQuery(id+"F0.imprint","IMPRINT",EDGE,{"disambiguationData":[TD([[subQ6,-1.0]])],"derivedFrom":subQ3}),1.0]])]});}
            var Q5;
            {var subQ9=sQuery(id+"F0.wireOp",EDGE,"E21.top");Q5=makeQuery(id+"F0.imprint","IMPRINT",FACE,{"disambiguationData":[TD([[makeQuery(id+"F0.imprint","IMPRINT",EDGE,{"derivedFrom":subQ9}),1.0]])]});}
            var Q6;
            {var subQ1=sQuery(id+"F0.wireOp",EDGE,"E4.top");Q6=makeQuery(id+"F0.imprint","IMPRINT",FACE,{"disambiguationData":[TD([[makeQuery(id+"F0.imprint","IMPRINT",EDGE,{"derivedFrom":subQ1}),1.0]])]});}
            var Q7;
            {var subQ5=sQuery(id+"F0.wireOp",EDGE,"E55.MirrorCS");Q7=makeQuery(id+"F0.imprint","IMPRINT",FACE,{"disambiguationData":[TD([[makeQuery(id+"F0.imprint","IMPRINT",EDGE,{"derivedFrom":subQ5}),-1.0]])]});}
            var Q8;
            {var subQ1=sQuery(id+"F0.wireOp",EDGE,"E37.MirrorCS");Q8=makeQuery(id+"F0.imprint","IMPRINT",FACE,{"disambiguationData":[TD([[makeQuery(id+"F0.imprint","IMPRINT",EDGE,{"derivedFrom":subQ1}),-1.0]])]});}
            var Q9;
            {var subQ0=sQuery(id+"F0.wireOp",EDGE,"E86.MirrorCS");var subQ1=sQuery(id+"F0.wireOp",EDGE,"E78.MirrorCS");var subQ2=makeQuery(id+"F0.imprint","INTERSECT",VERTEX,{"derivedFrom":[subQ1,subQ0]});Q9=makeQuery(id+"F0.imprint","IMPRINT",FACE,{"disambiguationData":[TD([[makeQuery(id+"F0.imprint","IMPRINT",EDGE,{"disambiguationData":[TD([[subQ2,-1.0]])],"derivedFrom":subQ1}),-1.0]])]});}
            var Q10;
            {var subQ0=sQuery(id+"F0.wireOp",EDGE,"E93.MirrorCS");var subQ1=sQuery(id+"F0.wireOp",EDGE,"E74.MirrorCS");var subQ2=makeQuery(id+"F0.imprint","INTERSECT",VERTEX,{"derivedFrom":[subQ1,subQ0]});Q10=makeQuery(id+"F0.imprint","IMPRINT",FACE,{"disambiguationData":[TD([[makeQuery(id+"F0.imprint","IMPRINT",EDGE,{"disambiguationData":[TD([[subQ2,-1.0]])],"derivedFrom":subQ1}),-1.0]])]});}
            var Q11;
            {var subQ0=sQuery(id+"F0.wireOp",EDGE,"E55.MirrorCS");Q11=makeQuery(id+"F0.imprint","IMPRINT",FACE,{"disambiguationData":[TD([[makeQuery(id+"F0.imprint","IMPRINT",EDGE,{"derivedFrom":subQ0}),1.0]])]});}
            var Q12;
            {var subQ0=sQuery(id+"F0.wireOp",EDGE,"E86.MirrorCS");var subQ1=sQuery(id+"F0.wireOp",EDGE,"E70.MirrorCS");var subQ2=makeQuery(id+"F0.imprint","INTERSECT",VERTEX,{"derivedFrom":[subQ1,subQ0]});Q12=makeQuery(id+"F0.imprint","IMPRINT",FACE,{"disambiguationData":[TD([[makeQuery(id+"F0.imprint","IMPRINT",EDGE,{"disambiguationData":[TD([[subQ2,-1.0]])],"derivedFrom":subQ1}),-1.0]])]});}
            var Q13;
            {var subQ0=sQuery(id+"F0.wireOp",EDGE,"E23.right");var subQ1=sQuery(id+"F0.wireOp",EDGE,"E2");var subQ2=makeQuery(id+"F0.imprint","INTERSECT",VERTEX,{"derivedFrom":[subQ1,subQ0]});Q13=makeQuery(id+"F0.imprint","IMPRINT",FACE,{"disambiguationData":[TD([[makeQuery(id+"F0.imprint","IMPRINT",EDGE,{"disambiguationData":[TD([[subQ2,-1.0]])],"derivedFrom":subQ1}),1.0]])]});}
            var Q14;
            {var subQ1=sQuery(id+"F0.wireOp",EDGE,"E2");var subQ7=sQuery(id+"F0.wireOp",EDGE,"E22.top");var subQ9=makeQuery(id+"F0.imprint","INTERSECT",VERTEX,{"derivedFrom":[subQ1,subQ7]});Q14=makeQuery(id+"F0.imprint","IMPRINT",FACE,{"disambiguationData":[TD([[makeQuery(id+"F0.imprint","IMPRINT",EDGE,{"disambiguationData":[TD([[subQ9,-1.0]])],"derivedFrom":subQ1}),1.0]])]});}
            var Q15;
            {var subQ0=sQuery(id+"F0.wireOp",EDGE,"E6");var subQ1=sQuery(id+"F0.wireOp",EDGE,"E5");var subQ2=makeQuery(id+"F0.imprint","INTERSECT",VERTEX,{"derivedFrom":[subQ1,subQ0]});Q15=makeQuery(id+"F0.imprint","IMPRINT",FACE,{"disambiguationData":[TD([[makeQuery(id+"F0.imprint","IMPRINT",EDGE,{"disambiguationData":[TD([[subQ2,1.0]])],"derivedFrom":subQ1}),1.0]])]});}
            var Q16;
            {var subQ3=sQuery(id+"F0.wireOp",EDGE,"E5");var subQ7=sQuery(id+"F0.wireOp",EDGE,"E26.right");var subQ9=makeQuery(id+"F0.imprint","INTERSECT",VERTEX,{"derivedFrom":[subQ3,subQ7]});Q16=makeQuery(id+"F0.imprint","IMPRINT",FACE,{"disambiguationData":[TD([[makeQuery(id+"F0.imprint","IMPRINT",EDGE,{"disambiguationData":[TD([[subQ9,1.0]])],"derivedFrom":subQ3}),1.0]])]});}
            var Q17;
            {var subQ5=sQuery(id+"F0.wireOp",EDGE,"E43.MirrorCS");var subQ7=sQuery(id+"F0.wireOp",EDGE,"E93.MirrorCS");var subQ9=makeQuery(id+"F0.imprint","INTERSECT",VERTEX,{"derivedFrom":[subQ5,subQ7]});Q17=makeQuery(id+"F0.imprint","IMPRINT",FACE,{"disambiguationData":[TD([[makeQuery(id+"F0.imprint","IMPRINT",EDGE,{"disambiguationData":[TD([[subQ9,-1.0]])],"derivedFrom":subQ5}),1.0]])]});}
            var Q18;
            {var subQ10=sQuery(id+"F0.wireOp",EDGE,"E59.MirrorCS");Q18=makeQuery(id+"F0.imprint","IMPRINT",FACE,{"disambiguationData":[TD([[makeQuery(id+"F0.imprint","IMPRINT",EDGE,{"derivedFrom":subQ10}),-1.0]])]});}
            var Q19;
            {var subQ0=sQuery(id+"F0.wireOp",EDGE,"E92.MirrorCS");var subQ3=sQuery(id+"F0.wireOp",EDGE,"E93.MirrorCS");var subQ5=makeQuery(id+"F0.imprint","INTERSECT",VERTEX,{"derivedFrom":[subQ0,subQ3]});Q19=makeQuery(id+"F0.imprint","IMPRINT",FACE,{"disambiguationData":[TD([[makeQuery(id+"F0.imprint","IMPRINT",EDGE,{"disambiguationData":[TD([[subQ5,1.0]])],"derivedFrom":subQ3}),-1.0]])]});}
            var Q20;
            {var subQ5=sQuery(id+"F0.wireOp",EDGE,"E60.MirrorCS");var subQ7=sQuery(id+"F0.wireOp",EDGE,"E68.MirrorCS");var subQ8=makeQuery(id+"F0.imprint","INTERSECT",VERTEX,{"derivedFrom":[subQ5,subQ7]});Q20=makeQuery(id+"F0.imprint","IMPRINT",FACE,{"disambiguationData":[TD([[makeQuery(id+"F0.imprint","IMPRINT",EDGE,{"disambiguationData":[TD([[subQ8,1.0]])],"derivedFrom":subQ5}),1.0]])]});}
            var Q21;
            {var subQ1=sQuery(id+"F0.wireOp",EDGE,"E91.MirrorCS");Q21=makeQuery(id+"F0.imprint","IMPRINT",FACE,{"disambiguationData":[TD([[makeQuery(id+"F0.imprint","IMPRINT",EDGE,{"derivedFrom":subQ1}),1.0]])]});}
            var Q22;
            {var subQ0=sQuery(id+"F0.wireOp",EDGE,"E84.MirrorCS");var subQ1=sQuery(id+"F0.wireOp",EDGE,"E74.MirrorCS");var subQ2=makeQuery(id+"F0.imprint","INTERSECT",VERTEX,{"derivedFrom":[subQ1,subQ0]});Q22=makeQuery(id+"F0.imprint","IMPRINT",FACE,{"disambiguationData":[TD([[makeQuery(id+"F0.imprint","IMPRINT",EDGE,{"disambiguationData":[TD([[subQ2,1.0]])],"derivedFrom":subQ1}),-1.0]])]});}
            var Q23;
            {var subQ0=sQuery(id+"F0.wireOp",EDGE,"E97.MirrorCS");var subQ1=sQuery(id+"F0.wireOp",EDGE,"E83.MirrorCS");var subQ2=makeQuery(id+"F0.imprint","INTERSECT",VERTEX,{"derivedFrom":[subQ1,subQ0]});Q23=makeQuery(id+"F0.imprint","IMPRINT",FACE,{"disambiguationData":[TD([[makeQuery(id+"F0.imprint","IMPRINT",EDGE,{"disambiguationData":[TD([[subQ2,-1.0]])],"derivedFrom":subQ1}),1.0]])]});}
            var Q24;
            {var subQ1=sQuery(id+"F0.wireOp",EDGE,"E2");var subQ3=sQuery(id+"F0.wireOp",EDGE,"E4.left");var subQ4=makeQuery(id+"F0.imprint","INTERSECT",VERTEX,{"derivedFrom":[subQ1,subQ3]});Q24=makeQuery(id+"F0.imprint","IMPRINT",FACE,{"disambiguationData":[TD([[makeQuery(id+"F0.imprint","IMPRINT",EDGE,{"disambiguationData":[TD([[subQ4,1.0]])],"derivedFrom":subQ3}),-1.0]])]});}
            var Q25;
            {var subQ0=sQuery(id+"F0.wireOp",EDGE,"E76.MirrorCS");var subQ1=sQuery(id+"F0.wireOp",EDGE,"E70.MirrorCS");var subQ2=makeQuery(id+"F0.imprint","INTERSECT",VERTEX,{"derivedFrom":[subQ1,subQ0]});Q25=makeQuery(id+"F0.imprint","IMPRINT",FACE,{"disambiguationData":[TD([[makeQuery(id+"F0.imprint","IMPRINT",EDGE,{"disambiguationData":[TD([[subQ2,-1.0]])],"derivedFrom":subQ1}),-1.0]])]});}
            var Q26;
            {var subQ0=sQuery(id+"F0.wireOp",EDGE,"E13.top");var subQ1=sQuery(id+"F0.wireOp",EDGE,"E2");var subQ2=makeQuery(id+"F0.imprint","INTERSECT",VERTEX,{"derivedFrom":[subQ1,subQ0]});Q26=makeQuery(id+"F0.imprint","IMPRINT",FACE,{"disambiguationData":[TD([[makeQuery(id+"F0.imprint","IMPRINT",EDGE,{"disambiguationData":[TD([[subQ2,-1.0]])],"derivedFrom":subQ1}),1.0]])]});}
            var Q27;
            {var subQ0=sQuery(id+"F0.wireOp",EDGE,"E13.right");Q27=makeQuery(id+"F0.imprint","IMPRINT",FACE,{"disambiguationData":[TD([[makeQuery(id+"F0.imprint","IMPRINT",EDGE,{"derivedFrom":subQ0}),1.0]])]});}
            var Q28;
            {var subQ0=sQuery(id+"F0.wireOp",EDGE,"E67.MirrorCS");Q28=makeQuery(id+"F0.imprint","IMPRINT",FACE,{"disambiguationData":[TD([[makeQuery(id+"F0.imprint","IMPRINT",EDGE,{"derivedFrom":subQ0}),-1.0]])]});}
            extrude(context, id + "F4", {"entities" : qUnion([Q0, Q1, Q2, Q3, Q4, Q5, Q6, Q7, Q8, Q9, Q10, Q11, Q12, Q13, Q14, Q15, Q16, Q17, Q18, Q19, Q20, Q21, Q22, Q23, Q24, Q25, Q26, Q27, Q28]), "depth" : 127 * mm, "offsetDistance" : 25.4 * mm});
        }
        {
            var Q0;
            {var subQ0=sQuery(id+"F0.wireOp",EDGE,"E104");Q0=makeQuery(id+"F0.imprint","IMPRINT",FACE,{"disambiguationData":[TD([[makeQuery(id+"F0.imprint","IMPRINT",EDGE,{"derivedFrom":subQ0}),1.0]])]});}
            var Q1;
            {var subQ5=sQuery(id+"F0.wireOp",EDGE,"E100");Q1=makeQuery(id+"F0.imprint","IMPRINT",FACE,{"disambiguationData":[TD([[makeQuery(id+"F0.imprint","IMPRINT",EDGE,{"derivedFrom":subQ5}),1.0]])]});}
            var Q2;
            {var subQ0=sQuery(id+"F0.wireOp",EDGE,"E99");var subQ1=sQuery(id+"F0.wireOp",EDGE,"E70.MirrorCS");var subQ2=makeQuery(id+"F0.imprint","INTERSECT",VERTEX,{"derivedFrom":[subQ1,subQ0]});Q2=makeQuery(id+"F0.imprint","IMPRINT",FACE,{"disambiguationData":[TD([[makeQuery(id+"F0.imprint","IMPRINT",EDGE,{"disambiguationData":[TD([[subQ2,-1.0]])],"derivedFrom":subQ1}),-1.0]])]});}
            var Q3;
            {var subQ5=sQuery(id+"F0.wireOp",EDGE,"E102");Q3=makeQuery(id+"F0.imprint","IMPRINT",FACE,{"disambiguationData":[TD([[makeQuery(id+"F0.imprint","IMPRINT",EDGE,{"derivedFrom":subQ5}),1.0]])]});}
            var Q4;
            {var subQ5=sQuery(id+"F0.wireOp",EDGE,"E110.MirrorCS");Q4=makeQuery(id+"F0.imprint","IMPRINT",FACE,{"disambiguationData":[TD([[makeQuery(id+"F0.imprint","IMPRINT",EDGE,{"derivedFrom":subQ5}),-1.0]])]});}
            var Q5;
            {var subQ0=sQuery(id+"F0.wireOp",EDGE,"E108.MirrorCS");var subQ1=sQuery(id+"F0.wireOp",EDGE,"E13.bottom");var subQ2=makeQuery(id+"F0.imprint","INTERSECT",VERTEX,{"derivedFrom":[subQ1,subQ0]});Q5=makeQuery(id+"F0.imprint","IMPRINT",FACE,{"disambiguationData":[TD([[makeQuery(id+"F0.imprint","IMPRINT",EDGE,{"disambiguationData":[TD([[subQ2,-1.0]])],"derivedFrom":subQ1}),1.0]])]});}
            var Q6;
            {var subQ5=sQuery(id+"F0.wireOp",EDGE,"E109.MirrorCS");Q6=makeQuery(id+"F0.imprint","IMPRINT",FACE,{"disambiguationData":[TD([[makeQuery(id+"F0.imprint","IMPRINT",EDGE,{"derivedFrom":subQ5}),-1.0]])]});}
            var Q7;
            {var subQ0=sQuery(id+"F0.wireOp",EDGE,"E111.MirrorCS");Q7=makeQuery(id+"F0.imprint","IMPRINT",FACE,{"disambiguationData":[TD([[makeQuery(id+"F0.imprint","IMPRINT",EDGE,{"derivedFrom":subQ0}),-1.0]])]});}
            extrude(context, id + "F5", {"entities" : qUnion([Q0, Q1, Q2, Q3, Q4, Q5, Q6, Q7]), "depth" : 50.8 * mm, "offsetDistance" : 25.4 * mm});
        }
        {
            var Q0;
            {var subQ1=sQuery(id+"F0.wireOp",EDGE,"E30.MirrorCS");Q0=makeQuery(id+"F0.imprint","IMPRINT",FACE,{"disambiguationData":[TD([[makeQuery(id+"F0.imprint","IMPRINT",EDGE,{"derivedFrom":subQ1}),1.0]])]});}
            var Q1;
            {var subQ0=sQuery(id+"F0.wireOp",EDGE,"E88.MirrorCS");var subQ3=sQuery(id+"F0.wireOp",EDGE,"E94.MirrorCS");var subQ5=makeQuery(id+"F0.imprint","INTERSECT",VERTEX,{"derivedFrom":[subQ0,subQ3]});Q1=makeQuery(id+"F0.imprint","IMPRINT",FACE,{"disambiguationData":[TD([[makeQuery(id+"F0.imprint","IMPRINT",EDGE,{"disambiguationData":[TD([[subQ5,-1.0]])],"derivedFrom":subQ0}),-1.0]])]});}
            var Q2;
            {var subQ0=sQuery(id+"F0.wireOp",EDGE,"E73.MirrorCS");Q2=makeQuery(id+"F0.imprint","IMPRINT",FACE,{"disambiguationData":[TD([[makeQuery(id+"F0.imprint","IMPRINT",EDGE,{"derivedFrom":subQ0}),1.0]])]});}
            var Q3;
            {var subQ14=sQuery(id+"F0.wireOp",EDGE,"E38.MirrorCS");Q3=makeQuery(id+"F0.imprint","IMPRINT",FACE,{"disambiguationData":[TD([[makeQuery(id+"F0.imprint","IMPRINT",EDGE,{"derivedFrom":subQ14}),-1.0]])]});}
            var Q4;
            {var subQ0=sQuery(id+"F0.wireOp",EDGE,"E84.MirrorCS");var subQ1=sQuery(id+"F0.wireOp",EDGE,"E81.MirrorCS");var subQ2=makeQuery(id+"F0.imprint","INTERSECT",VERTEX,{"derivedFrom":[subQ1,subQ0]});Q4=makeQuery(id+"F0.imprint","IMPRINT",FACE,{"disambiguationData":[TD([[makeQuery(id+"F0.imprint","IMPRINT",EDGE,{"disambiguationData":[TD([[subQ2,1.0]])],"derivedFrom":subQ1}),-1.0]])]});}
            var Q5;
            {var subQ15=sQuery(id+"F0.wireOp",EDGE,"E63.MirrorCS");Q5=makeQuery(id+"F0.imprint","IMPRINT",FACE,{"disambiguationData":[TD([[makeQuery(id+"F0.imprint","IMPRINT",EDGE,{"derivedFrom":subQ15}),-1.0]])]});}
            var Q6;
            {var subQ6=sQuery(id+"F0.wireOp",EDGE,"E102");Q6=makeQuery(id+"F0.imprint","IMPRINT",FACE,{"disambiguationData":[TD([[makeQuery(id+"F0.imprint","IMPRINT",EDGE,{"derivedFrom":subQ6}),-1.0]])]});}
            var Q7;
            {var subQ10=sQuery(id+"F0.wireOp",EDGE,"E110.MirrorCS");Q7=makeQuery(id+"F0.imprint","IMPRINT",FACE,{"disambiguationData":[TD([[makeQuery(id+"F0.imprint","IMPRINT",EDGE,{"derivedFrom":subQ10}),1.0]])]});}
            var Q8;
            {var subQ5=sQuery(id+"F0.wireOp",EDGE,"E3.left");Q8=makeQuery(id+"F0.imprint","IMPRINT",FACE,{"disambiguationData":[TD([[makeQuery(id+"F0.imprint","IMPRINT",EDGE,{"derivedFrom":subQ5}),1.0]])]});}
            var Q9;
            {var subQ3=sQuery(id+"F0.wireOp",EDGE,"E11.left");Q9=makeQuery(id+"F0.imprint","IMPRINT",FACE,{"disambiguationData":[TD([[makeQuery(id+"F0.imprint","IMPRINT",EDGE,{"derivedFrom":subQ3}),1.0]])]});}
            var Q10;
            {var subQ3=sQuery(id+"F0.wireOp",EDGE,"E98.MirrorCS");Q10=makeQuery(id+"F0.imprint","IMPRINT",FACE,{"disambiguationData":[TD([[makeQuery(id+"F0.imprint","IMPRINT",EDGE,{"derivedFrom":subQ3}),-1.0]])]});}
            var Q11;
            {var subQ3=sQuery(id+"F0.wireOp",EDGE,"E23.left");var subQ5=sQuery(id+"F0.wireOp",EDGE,"E2");var subQ7=makeQuery(id+"F0.imprint","INTERSECT",VERTEX,{"derivedFrom":[subQ5,subQ3]});Q11=makeQuery(id+"F0.imprint","IMPRINT",FACE,{"disambiguationData":[TD([[makeQuery(id+"F0.imprint","IMPRINT",EDGE,{"disambiguationData":[TD([[subQ7,-1.0]])],"derivedFrom":subQ5}),-1.0]])]});}
            var Q12;
            {var subQ8=sQuery(id+"F0.wireOp",EDGE,"E10.left");Q12=makeQuery(id+"F0.imprint","IMPRINT",FACE,{"disambiguationData":[TD([[makeQuery(id+"F0.imprint","IMPRINT",EDGE,{"derivedFrom":subQ8}),1.0]])]});}
            var Q13;
            {var subQ0=sQuery(id+"F0.wireOp",EDGE,"E10.right");Q13=makeQuery(id+"F0.imprint","IMPRINT",FACE,{"disambiguationData":[TD([[makeQuery(id+"F0.imprint","IMPRINT",EDGE,{"derivedFrom":subQ0}),-1.0]])]});}
            var Q14;
            {var subQ0=sQuery(id+"F0.wireOp",EDGE,"E4.left");var subQ3=sQuery(id+"F0.wireOp",EDGE,"E10.top");var subQ5=makeQuery(id+"F0.imprint","INTERSECT",VERTEX,{"derivedFrom":[subQ0,subQ3]});Q14=makeQuery(id+"F0.imprint","IMPRINT",FACE,{"disambiguationData":[TD([[makeQuery(id+"F0.imprint","IMPRINT",EDGE,{"disambiguationData":[TD([[subQ5,-1.0]])],"derivedFrom":subQ3}),1.0]])]});}
            var Q15;
            {var subQ3=sQuery(id+"F0.wireOp",EDGE,"E12.right");Q15=makeQuery(id+"F0.imprint","IMPRINT",FACE,{"disambiguationData":[TD([[makeQuery(id+"F0.imprint","IMPRINT",EDGE,{"derivedFrom":subQ3}),-1.0]])]});}
            extrude(context, id + "F6", {"entities" : qUnion([Q0, Q1, Q2, Q3, Q4, Q5, Q6, Q7, Q8, Q9, Q10, Q11, Q12, Q13, Q14, Q15]), "depth" : 76.2 * mm, "offsetDistance" : 25.4 * mm});
        }
    });
